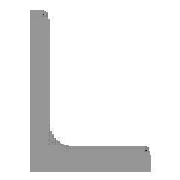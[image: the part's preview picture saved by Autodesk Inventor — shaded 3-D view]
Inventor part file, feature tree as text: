
AUTODESK INVENTOR PART (.ipt)
format: ipt  version: 2024.1 (Build 281209000, 209)  size: 133,120 bytes
history: native  units: mm (DEFAULTED — no unit token found)
features: other x4, plane x3, split x2, sketch x1
ambient origin geometry x8: Origin, YZ Plane, XZ Plane, XY Plane, X Axis, Y Axis, Z Axis, Center Point
bodies: Solid1 (feature_tree), Body (feature_tree)
feature tree (10):
  parser-record x1  (decoder bookkeeping rows leaked as tree rows — omitted from the tree; the rows remain in map.json)
  other  "Driven Length"
  other  "Start Plane"
  other  "End Plane"
  plane  "Work Plane4"
  split  "Split1"
  plane  "Work Plane5"
  split  "Split2"
  sketch  "Sketch3"  dims[d0=25.4mm d1=25.4mm d2=3.175mm d3=3.175mm d4=1025.4mm d5=0.0mm d10=0.0mm d11=0.0mm d12=-12.7mm d13=1012.7mm d14=3.302mm d15=1.524mm d16=90.0deg d17=1025.4mm]
  plane  "Work Plane3"
